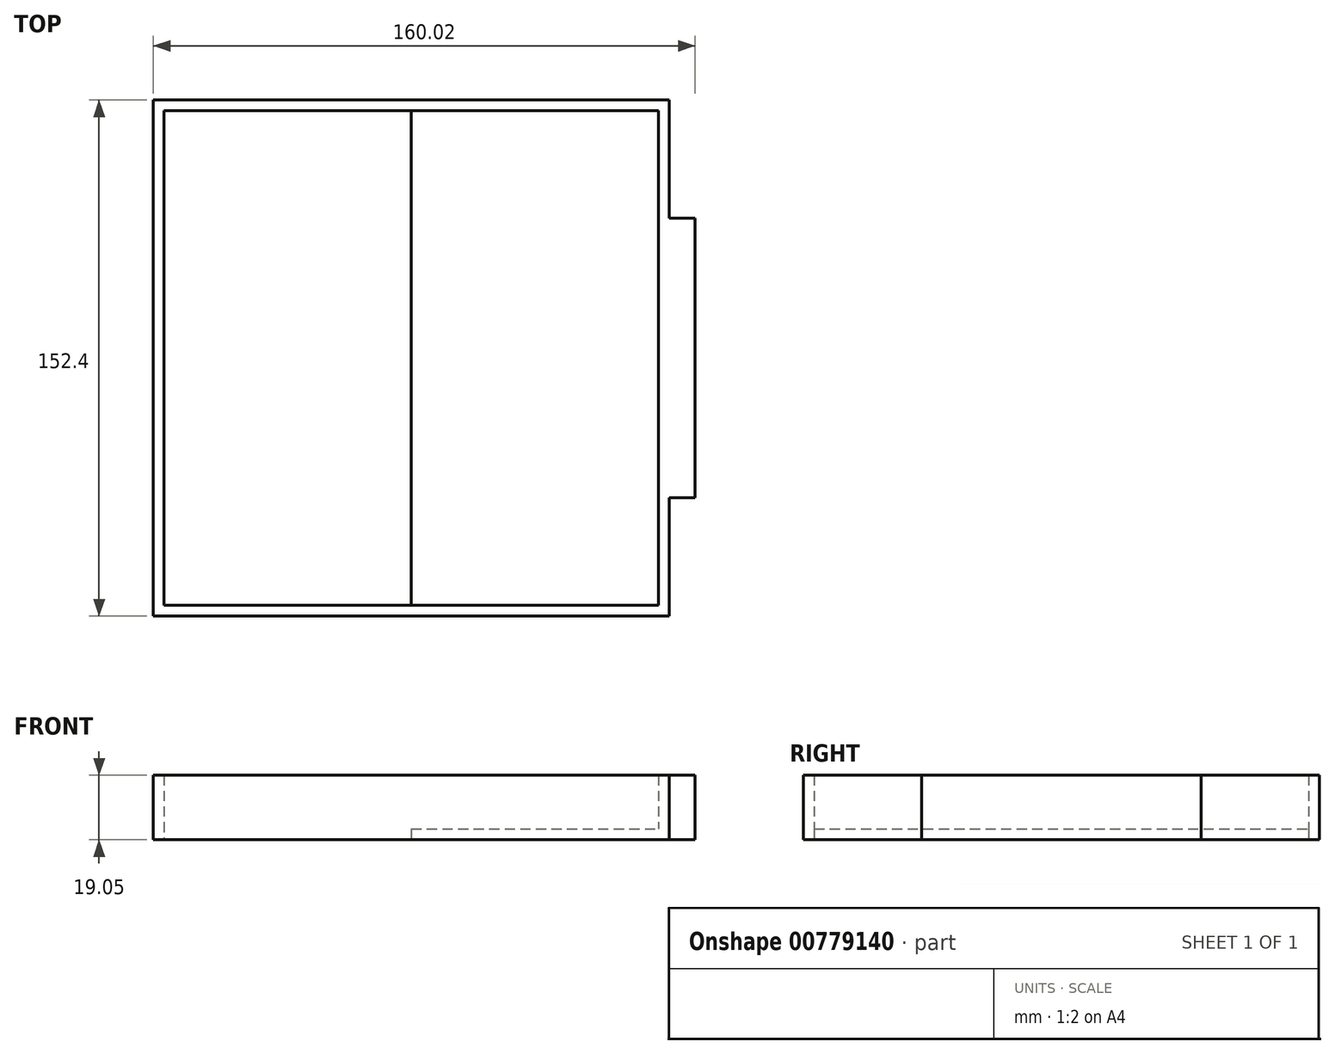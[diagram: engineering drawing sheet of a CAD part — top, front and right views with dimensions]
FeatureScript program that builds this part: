
annotation { "Feature Type Name" : "Feature", "Feature Type Description" : "" }
export const myFeature = defineFeature(function(context is Context, id is Id, definition is map)
    precondition{}
    {
        {
            var Q0;
            Q0=qCreatedBy(makeId("Top.planeOp"),FACE);
            var sketch = newSketch(context, id + "F0", { "sketchPlane" : qUnion([Q0])});
            skLineSegment(sketch, "E0.bottom", {"start": v(76.2, 76.2) * mm, "end": v(-76.2, 76.2) * mm});
            skLineSegment(sketch, "E0.top", {"start": v(76.2, -76.2) * mm, "end": v(-76.2, -76.2) * mm});
            skLineSegment(sketch, "E0.right", {"start": v(-76.2, 76.2) * mm, "end": v(-76.2, -76.2) * mm});
            skLineSegment(sketch, "E1", {"start": v(76.2, 76.2) * mm, "end": v(76.2, -76.2) * mm});
            skLineSegment(sketch, "E2.bottom", {"start": v(-76.2, 76.2) * mm, "end": v(-73.02, 76.2) * mm});
            skLineSegment(sketch, "E2.top", {"start": v(-76.2, -76.2) * mm, "end": v(-73.02, -76.2) * mm});
            skLineSegment(sketch, "E2.right", {"start": v(-73.02, 76.2) * mm, "end": v(-73.02, -76.2) * mm});
            skLineSegment(sketch, "E3.MirrorCS", {"start": v(73.02, 76.2) * mm, "end": v(73.02, -76.2) * mm});
            skLineSegment(sketch, "E4.MirrorCS", {"start": v(76.2, -76.2) * mm, "end": v(73.02, -76.2) * mm});
            skLineSegment(sketch, "E5.bottom", {"start": v(-73.02, 76.2) * mm, "end": v(73.02, 76.2) * mm});
            skLineSegment(sketch, "E5.top", {"start": v(-73.02, 73.02) * mm, "end": v(73.02, 73.02) * mm});
            skLineSegment(sketch, "E5.left", {"start": v(-73.02, 76.2) * mm, "end": v(-73.02, 73.02) * mm});
            skLineSegment(sketch, "E5.right", {"start": v(73.02, 76.2) * mm, "end": v(73.02, 73.02) * mm});
            skLineSegment(sketch, "E6.MirrorCS", {"start": v(-73.02, -73.02) * mm, "end": v(73.02, -73.02) * mm});
            skSolve(sketch);
        }
        {
            var Q0;
            {var subQ3=sQuery(id+"F0.wireOp",EDGE,"E0.right");Q0=makeQuery(id+"F0.imprint","IMPRINT",FACE,{"disambiguationData":[TD([[makeQuery(id+"F0.imprint","IMPRINT",EDGE,{"derivedFrom":subQ3}),1.0]])]});}
            var Q1;
            {var subQ5=sQuery(id+"F0.wireOp",EDGE,"E5.top");Q1=makeQuery(id+"F0.imprint","IMPRINT",FACE,{"disambiguationData":[TD([[makeQuery(id+"F0.imprint","IMPRINT",EDGE,{"derivedFrom":subQ5}),1.0]])]});}
            var Q2;
            {var subQ0=sQuery(id+"F0.wireOp",EDGE,"E1");Q2=makeQuery(id+"F0.imprint","IMPRINT",FACE,{"disambiguationData":[TD([[makeQuery(id+"F0.imprint","IMPRINT",EDGE,{"derivedFrom":subQ0}),-1.0]])]});}
            var Q3;
            {var subQ5=sQuery(id+"F0.wireOp",EDGE,"E6.MirrorCS");Q3=makeQuery(id+"F0.imprint","IMPRINT",FACE,{"disambiguationData":[TD([[makeQuery(id+"F0.imprint","IMPRINT",EDGE,{"derivedFrom":subQ5}),-1.0]])]});}
            extrude(context, id + "F1", {"entities" : qUnion([Q0, Q1, Q2, Q3]), "depth" : 19.05 * mm, "offsetDistance" : 25.4 * mm});
        }
        {
            var Q0;
            Q0=qCreatedBy(makeId("Top.planeOp"),FACE);
            var sketch = newSketch(context, id + "F2", { "sketchPlane" : qUnion([Q0])});
            skLineSegment(sketch, "E7.bottom", {"start": v(0, -73.03) * mm, "end": v(73.03, -73.03) * mm});
            skLineSegment(sketch, "E7.top", {"start": v(0, 73.03) * mm, "end": v(73.02, 73.03) * mm});
            skLineSegment(sketch, "E7.left", {"start": v(0, -73.03) * mm, "end": v(0, 73.03) * mm});
            skLineSegment(sketch, "E7.right", {"start": v(73.03, -73.03) * mm, "end": v(73.03, 73.03) * mm});
            skSolve(sketch);
        }
        {
            var Q0;
            Q0=makeQuery(id+"F2.imprint","IMPRINT",FACE,{"disambiguationData":[TD([[makeQuery(id+"F2.imprint","IMPRINT",EDGE,{"derivedFrom":sQuery(id+"F2.wireOp",EDGE,"E7.bottom")}),1.0]])]});
            extrude(context, id + "F3", {"entities" : qUnion([Q0]), "operationType" : NewBodyOperationType.ADD, "depth" : 3.17 * mm, "offsetDistance" : 25.4 * mm});
        }
        {
            var Q0;
            Q0=qCreatedBy(makeId("Top.planeOp"),FACE);
            var sketch = newSketch(context, id + "F4", { "sketchPlane" : qUnion([Q0])});
            skLineSegment(sketch, "E8.bottom", {"start": v(76.2, 41.28) * mm, "end": v(83.82, 41.28) * mm});
            skLineSegment(sketch, "E8.top", {"start": v(76.2, -41.28) * mm, "end": v(83.82, -41.28) * mm});
            skLineSegment(sketch, "E8.left", {"start": v(76.2, 41.28) * mm, "end": v(76.2, -41.28) * mm});
            skLineSegment(sketch, "E8.right", {"start": v(83.82, 41.28) * mm, "end": v(83.82, -41.28) * mm});
            skSolve(sketch);
        }
        {
            var Q0;
            Q0=makeQuery(id+"F4.imprint","IMPRINT",FACE,{"disambiguationData":[TD([[makeQuery(id+"F4.imprint","IMPRINT",EDGE,{"derivedFrom":sQuery(id+"F4.wireOp",EDGE,"E8.bottom")}),-1.0]])]});
            extrude(context, id + "F5", {"entities" : qUnion([Q0]), "operationType" : NewBodyOperationType.ADD, "depth" : 19.05 * mm, "offsetDistance" : 25.4 * mm});
        }
    });
